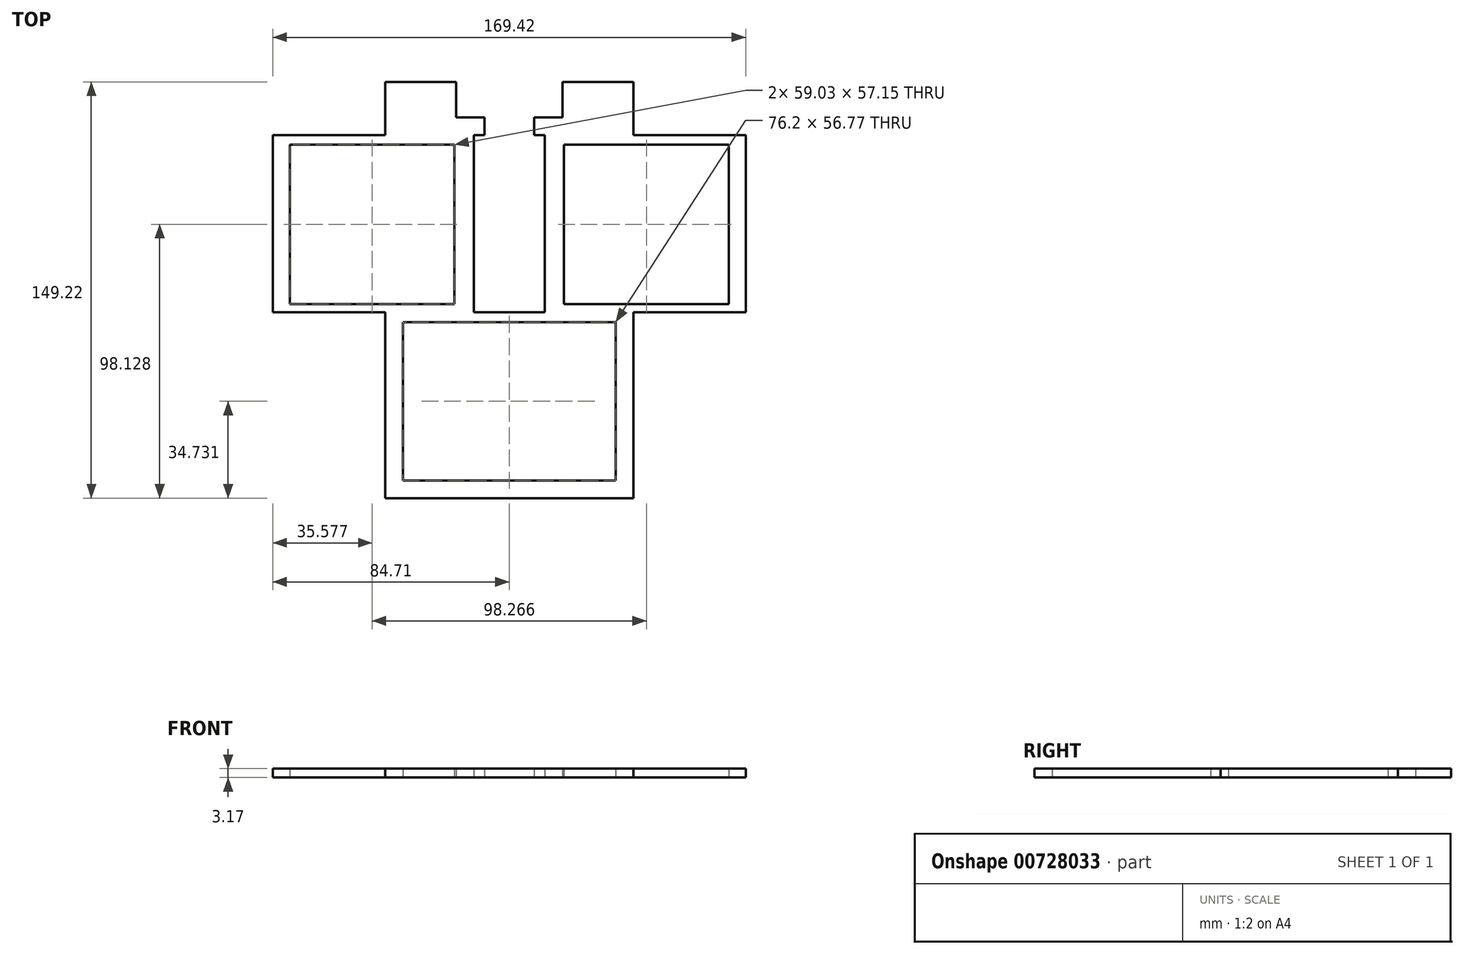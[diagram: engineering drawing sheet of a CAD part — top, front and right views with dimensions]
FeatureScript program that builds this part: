
annotation { "Feature Type Name" : "Feature", "Feature Type Description" : "" }
export const myFeature = defineFeature(function(context is Context, id is Id, definition is map)
    precondition{}
    {
        {
            var Q0;
            Q0=qCreatedBy(makeId("Top.planeOp"),FACE);
            var sketch = newSketch(context, id + "F0", { "sketchPlane" : qUnion([Q0])});
            skLineSegment(sketch, "E0", {"start": v(-25.4, -60.33) * mm, "end": v(50.8, -60.33) * mm});
            skLineSegment(sketch, "E1", {"start": v(-2.16, 0) * mm, "end": v(0, 0) * mm});
            skLineSegment(sketch, "E2", {"start": v(-2.16, 0) * mm, "end": v(27.56, 0) * mm});
            skLineSegment(sketch, "E3.top", {"start": v(-2.16, 63.5) * mm, "end": v(-72, 63.5) * mm});
            skLineSegment(sketch, "E3.left", {"start": v(-2.16, 0) * mm, "end": v(-2.16, 63.5) * mm});
            skLineSegment(sketch, "E3.right", {"start": v(-72, 0) * mm, "end": v(-72, 63.5) * mm});
            skLineSegment(sketch, "E4", {"start": v(0, 0) * mm, "end": v(0, 63.5) * mm});
            skLineSegment(sketch, "E5", {"start": v(0, 63.5) * mm, "end": v(-2.16, 63.5) * mm});
            skLineSegment(sketch, "E6.left", {"start": v(0, 63.5) * mm, "end": v(0, 69.85) * mm});
            skLineSegment(sketch, "E7", {"start": v(0, 69.85) * mm, "end": v(-31.75, 69.85) * mm});
            skLineSegment(sketch, "E8", {"start": v(-31.75, 69.85) * mm, "end": v(-31.75, 63.5) * mm});
            skLineSegment(sketch, "E9.bottom", {"start": v(-31.75, 69.85) * mm, "end": v(-6.35, 69.85) * mm});
            skLineSegment(sketch, "E9.top", {"start": v(-31.75, 82.55) * mm, "end": v(-6.35, 82.55) * mm});
            skLineSegment(sketch, "E9.left", {"start": v(-31.75, 69.85) * mm, "end": v(-31.75, 82.55) * mm});
            skLineSegment(sketch, "E9.right", {"start": v(-6.35, 69.85) * mm, "end": v(-6.35, 82.55) * mm});
            skLineSegment(sketch, "E10.bottom", {"start": v(-65.95, 60.03) * mm, "end": v(-6.92, 60.03) * mm});
            skLineSegment(sketch, "E10.top", {"start": v(-65.95, 2.88) * mm, "end": v(-6.92, 2.88) * mm});
            skLineSegment(sketch, "E10.left", {"start": v(-65.95, 60.03) * mm, "end": v(-65.95, 2.88) * mm});
            skLineSegment(sketch, "E10.right", {"start": v(-6.92, 60.03) * mm, "end": v(-6.92, 2.88) * mm});
            skLineSegment(sketch, "E11.MirrorCS", {"start": v(27.56, 0) * mm, "end": v(27.56, 63.5) * mm});
            skLineSegment(sketch, "E12.MirrorCS", {"start": v(25.4, 0) * mm, "end": v(25.4, 63.5) * mm});
            skLineSegment(sketch, "E13.MirrorCS", {"start": v(57.15, 69.85) * mm, "end": v(31.75, 69.85) * mm});
            skLineSegment(sketch, "E14.MirrorCS", {"start": v(25.4, 63.5) * mm, "end": v(27.56, 63.5) * mm});
            skLineSegment(sketch, "E15.MirrorCS", {"start": v(25.4, 63.5) * mm, "end": v(21.6, 63.5) * mm});
            skLineSegment(sketch, "E16.MirrorCS", {"start": v(57.15, 82.55) * mm, "end": v(31.75, 82.55) * mm});
            skLineSegment(sketch, "E17.MirrorCS", {"start": v(57.15, 69.85) * mm, "end": v(57.15, 82.55) * mm});
            skLineSegment(sketch, "E18.MirrorCS", {"start": v(31.75, 69.85) * mm, "end": v(31.75, 82.55) * mm});
            skLineSegment(sketch, "E19.MirrorCS", {"start": v(25.4, 69.85) * mm, "end": v(57.15, 69.85) * mm});
            skLineSegment(sketch, "E20.MirrorCS", {"start": v(25.4, 69.85) * mm, "end": v(21.6, 69.85) * mm});
            skLineSegment(sketch, "E21.MirrorCS", {"start": v(25.4, 63.5) * mm, "end": v(25.4, 69.85) * mm});
            skLineSegment(sketch, "E22.MirrorCS", {"start": v(57.15, 69.85) * mm, "end": v(57.15, 63.5) * mm});
            skLineSegment(sketch, "E23.bottom", {"start": v(0, 69.85) * mm, "end": v(3.81, 69.85) * mm});
            skLineSegment(sketch, "E23.top", {"start": v(0, 63.5) * mm, "end": v(3.81, 63.5) * mm});
            skLineSegment(sketch, "E23.left", {"start": v(0, 69.85) * mm, "end": v(0, 63.5) * mm});
            skLineSegment(sketch, "E23.right", {"start": v(3.81, 69.85) * mm, "end": v(3.81, 63.5) * mm});
            skLineSegment(sketch, "E24", {"start": v(12.7, 0) * mm, "end": v(12.7, 57.08) * mm});
            skLineSegment(sketch, "E25.MirrorCS", {"start": v(21.6, 69.85) * mm, "end": v(21.6, 63.5) * mm});
            skLineSegment(sketch, "E26.MirrorCS", {"start": v(32.32, 60.03) * mm, "end": v(32.32, 2.88) * mm});
            skLineSegment(sketch, "E27.MirrorCS", {"start": v(91.35, 60.03) * mm, "end": v(32.32, 60.03) * mm});
            skLineSegment(sketch, "E28.MirrorCS", {"start": v(91.35, 60.03) * mm, "end": v(91.35, 2.88) * mm});
            skLineSegment(sketch, "E29.MirrorCS", {"start": v(91.35, 2.88) * mm, "end": v(32.32, 2.88) * mm});
            skLineSegment(sketch, "E30.MirrorCS", {"start": v(50.8, 0) * mm, "end": v(97.4, 0) * mm});
            skLineSegment(sketch, "E31.MirrorCS", {"start": v(97.4, 0) * mm, "end": v(97.4, 63.5) * mm});
            skLineSegment(sketch, "E32.MirrorCS", {"start": v(27.56, 63.5) * mm, "end": v(97.4, 63.5) * mm});
            skPoint(sketch, "E33.start.orphan", {"position": v(-19.05, 0) * mm});
            skPoint(sketch, "E34.end.orphan", {"position": v(-25.4, 0) * mm});
            skLineSegment(sketch, "E35", {"start": v(-25.4, -3.55) * mm, "end": v(-25.4, -60.33) * mm});
            skLineSegment(sketch, "E36", {"start": v(50.8, -3.55) * mm, "end": v(50.8, -60.33) * mm});
            skLineSegment(sketch, "E37", {"start": v(-31.75, 0) * mm, "end": v(-31.75, -66.68) * mm});
            skLineSegment(sketch, "E38", {"start": v(-31.75, -66.68) * mm, "end": v(57.15, -66.67) * mm});
            skLineSegment(sketch, "E39", {"start": v(57.15, -66.67) * mm, "end": v(57.15, 0) * mm});
            skLineSegment(sketch, "E40", {"start": v(-25.4, -3.55) * mm, "end": v(50.8, -3.55) * mm});
            skLineSegment(sketch, "E41.trimOffspring", {"start": v(-25.4, 0) * mm, "end": v(-72, 0) * mm});
            skPoint(sketch, "E42.orphan", {"position": v(27.56, 0) * mm});
            skSolve(sketch);
        }
        {
            var Q0;
            Q0 = qSketchRegion(id + "F0", true);
            extrude(context, id + "F1", {"entities" : qUnion([Q0]), "depth" : 3.17 * mm, "offsetDistance" : 25.4 * mm});
        }
    });
